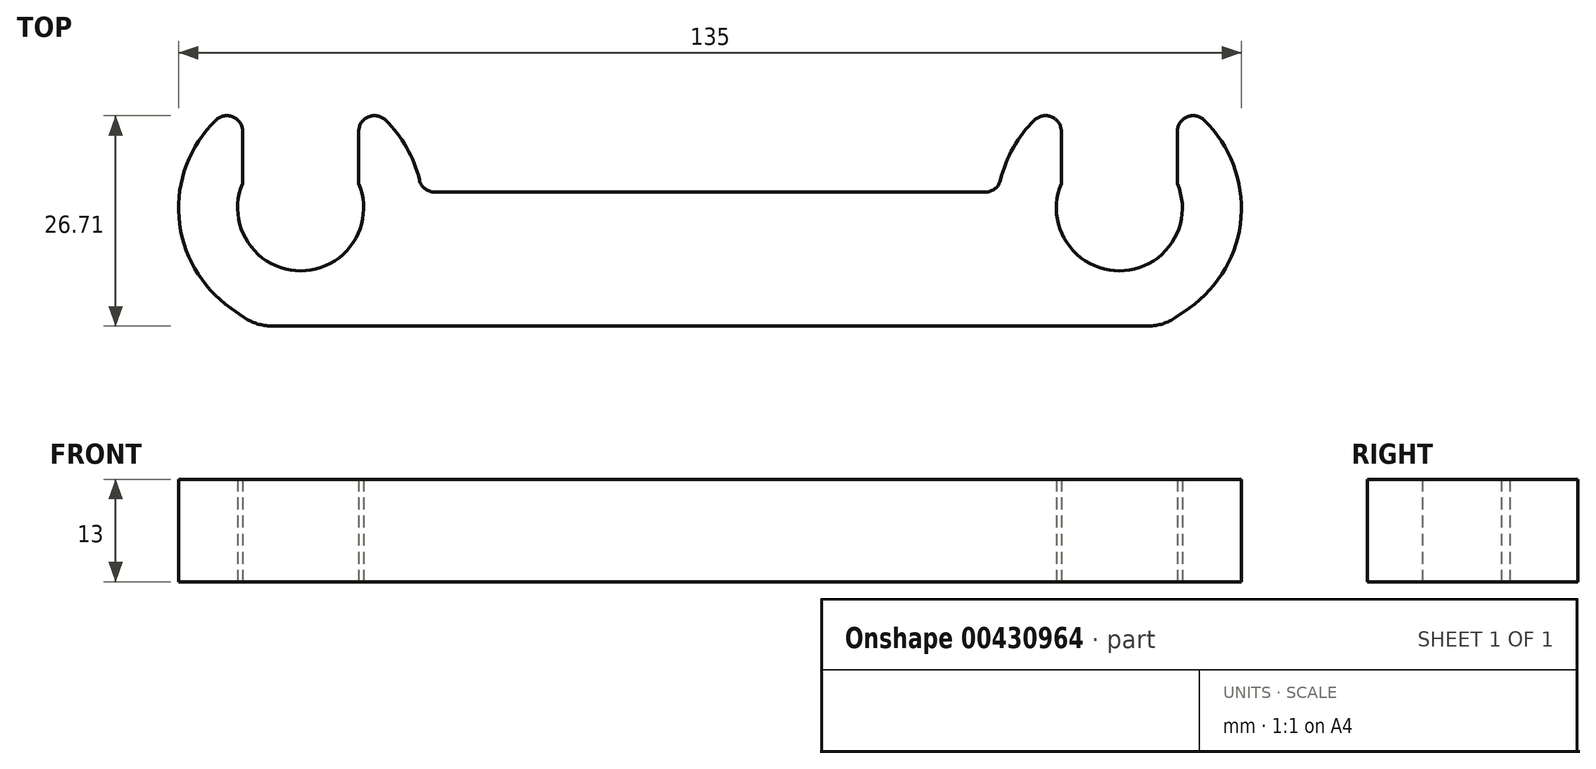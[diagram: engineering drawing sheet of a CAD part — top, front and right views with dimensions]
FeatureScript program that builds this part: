
annotation { "Feature Type Name" : "Feature", "Feature Type Description" : "" }
export const myFeature = defineFeature(function(context is Context, id is Id, definition is map)
    precondition{}
    {
        {
            var Q0;
            Q0=qCreatedBy(makeId("Top.planeOp"),FACE);
            var sketch = newSketch(context, id + "F0", { "sketchPlane" : qUnion([Q0])});
            skArc(sketch, "E0", {"start": v(-62.76, 14.15) * mm, "mid": v(-67.45, 1.79) * mm, "end": v(-60.9, -9.7) * mm});
            skLineSegment(sketch, "E1.0", {"start": v(-34.96, 5) * mm, "end": v(0, 5) * mm});
            skLineSegment(sketch, "E2.0", {"start": v(-55.7, -12) * mm, "end": v(0, -12) * mm});
            skLineSegment(sketch, "E3.0", {"start": v(-59.38, 6.1) * mm, "end": v(-59.38, 12.71) * mm});
            skLineSegment(sketch, "E4.0", {"start": v(-44.63, 6.1) * mm, "end": v(-44.63, 12.71) * mm});
            skArc(sketch, "E5.trimOffspring", {"start": v(-36.91, 6.54) * mm, "mid": v(-38.52, 10.66) * mm, "end": v(-41.24, 14.15) * mm});
            skLineSegment(sketch, "E6", {"start": v(0, 5) * mm, "end": v(0, -12) * mm, "construction": true});
            skPoint(sketch, "E7.visualSharp", {"position": v(-36.63, 5) * mm});
            skArc(sketch, "E7.filletArc", {"start": v(-36.91, 6.54) * mm, "mid": v(-36.2, 5.43) * mm, "end": v(-34.96, 5) * mm});
            skPoint(sketch, "E8.visualSharp", {"position": v(-44.63, 16.63) * mm});
            skArc(sketch, "E8.filletArc", {"start": v(-41.24, 14.15) * mm, "mid": v(-43.4, 14.55) * mm, "end": v(-44.62, 12.71) * mm});
            skPoint(sketch, "E9.visualSharp", {"position": v(-59.38, 16.63) * mm});
            skArc(sketch, "E9.filletArc", {"start": v(-59.38, 12.71) * mm, "mid": v(-60.6, 14.55) * mm, "end": v(-62.76, 14.15) * mm});
            skArc(sketch, "E10", {"start": v(-59.38, 6.1) * mm, "mid": v(-52, -5) * mm, "end": v(-44.62, 6.1) * mm});
            skLineSegment(sketch, "E11", {"start": v(-60.9, -9.7) * mm, "end": v(-59.15, -10.91) * mm});
            skPoint(sketch, "E12.visualSharp", {"position": v(-57.6, -12) * mm});
            skArc(sketch, "E12.filletArc", {"start": v(-59.15, -10.91) * mm, "mid": v(-57.51, -11.72) * mm, "end": v(-55.7, -12) * mm});
            skArc(sketch, "E13.MirrorCS", {"start": v(36.91, 6.54) * mm, "mid": v(36.2, 5.43) * mm, "end": v(34.96, 5) * mm});
            skLineSegment(sketch, "E14.MirrorCS", {"start": v(60.9, -9.7) * mm, "end": v(59.15, -10.91) * mm});
            skArc(sketch, "E15.MirrorCS", {"start": v(59.15, -10.91) * mm, "mid": v(57.51, -11.72) * mm, "end": v(55.7, -12) * mm});
            skPoint(sketch, "E16.MirrorP", {"position": v(59.38, 16.63) * mm});
            skPoint(sketch, "E17.MirrorP", {"position": v(44.63, 16.63) * mm});
            skLineSegment(sketch, "E18.MirrorCS", {"start": v(34.96, 5) * mm, "end": v(0, 5) * mm});
            skPoint(sketch, "E19.MirrorP", {"position": v(57.6, -12) * mm});
            skLineSegment(sketch, "E20.MirrorCS", {"start": v(59.38, 6.1) * mm, "end": v(59.38, 12.71) * mm});
            skLineSegment(sketch, "E21.MirrorCS", {"start": v(55.7, -12) * mm, "end": v(0, -12) * mm});
            skLineSegment(sketch, "E22.MirrorCS", {"start": v(44.63, 6.1) * mm, "end": v(44.63, 12.71) * mm});
            skArc(sketch, "E23.MirrorCS", {"start": v(36.91, 6.54) * mm, "mid": v(38.52, 10.66) * mm, "end": v(41.24, 14.15) * mm});
            skPoint(sketch, "E24.MirrorP", {"position": v(36.63, 5) * mm});
            skArc(sketch, "E25.MirrorCS", {"start": v(41.24, 14.15) * mm, "mid": v(43.4, 14.55) * mm, "end": v(44.62, 12.71) * mm});
            skArc(sketch, "E26.MirrorCS", {"start": v(59.38, 6.1) * mm, "mid": v(52, -5) * mm, "end": v(44.62, 6.1) * mm});
            skArc(sketch, "E27.MirrorCS", {"start": v(59.38, 12.71) * mm, "mid": v(60.6, 14.55) * mm, "end": v(62.76, 14.15) * mm});
            skArc(sketch, "E28.MirrorCS", {"start": v(62.76, 14.15) * mm, "mid": v(67.45, 1.79) * mm, "end": v(60.9, -9.7) * mm});
            skSolve(sketch);
        }
        {
            var Q0;
            Q0 = qSketchRegion(id + "F0", true);
            extrude(context, id + "F1", {"entities" : qUnion([Q0]), "depth" : 13 * mm});
        }
    });
